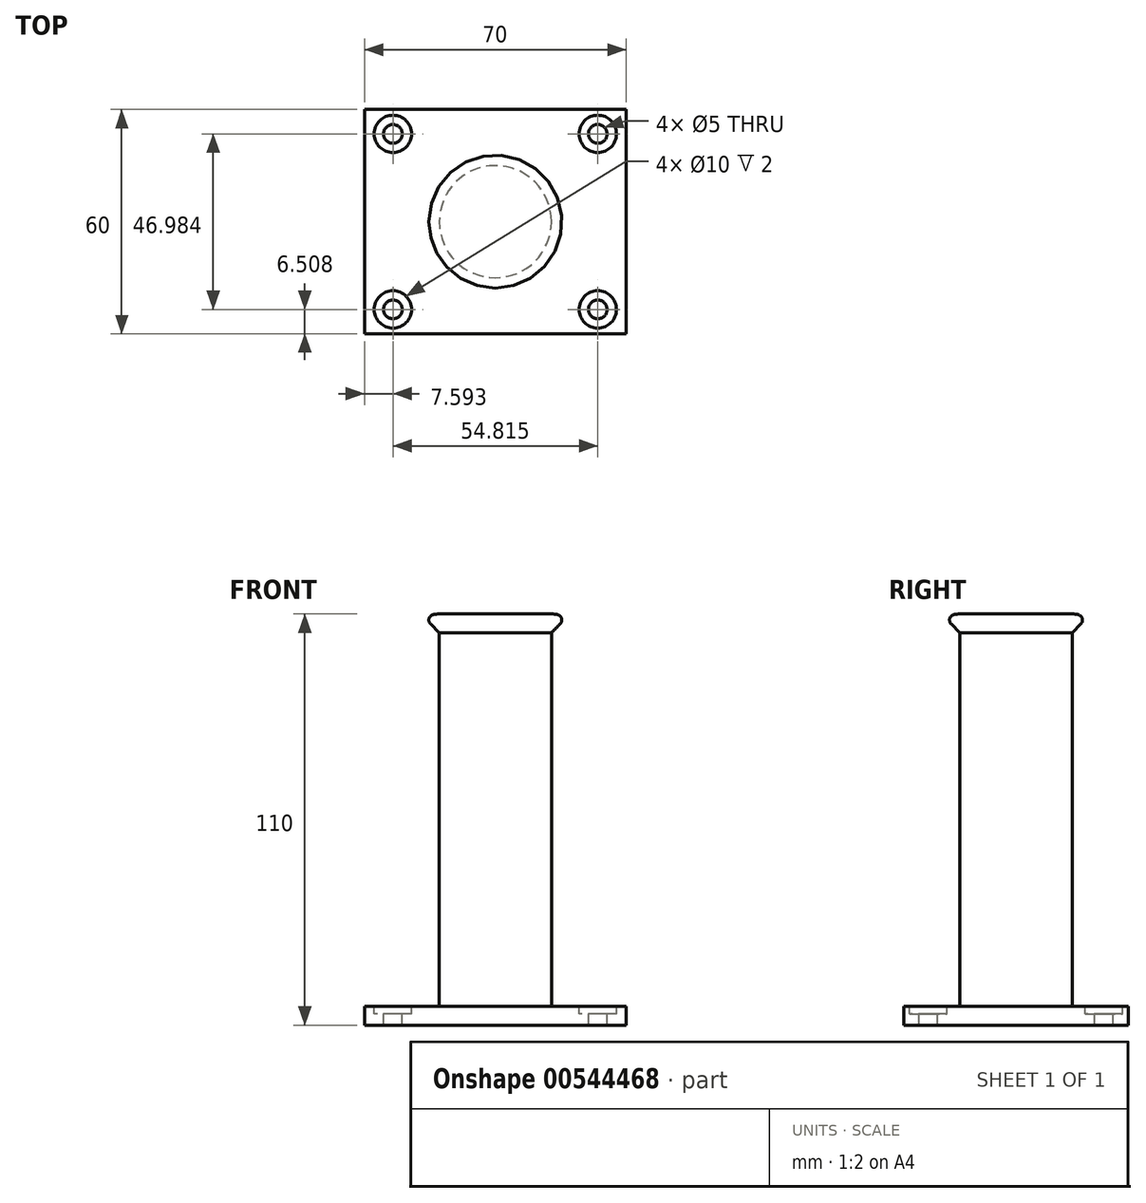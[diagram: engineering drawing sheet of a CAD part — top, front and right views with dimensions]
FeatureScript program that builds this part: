
annotation { "Feature Type Name" : "Feature", "Feature Type Description" : "" }
export const myFeature = defineFeature(function(context is Context, id is Id, definition is map)
    precondition{}
    {
        {
            var Q0;
            Q0=qCreatedBy(makeId("Top.planeOp"),FACE);
            var sketch = newSketch(context, id + "F0", { "sketchPlane" : qUnion([Q0])});
            skLineSegment(sketch, "E0.bottom", {"start": v(35, 30) * mm, "end": v(-35, 30) * mm});
            skLineSegment(sketch, "E0.top", {"start": v(35, -30) * mm, "end": v(-35, -30) * mm});
            skLineSegment(sketch, "E0.left", {"start": v(35, 30) * mm, "end": v(35, -30) * mm});
            skLineSegment(sketch, "E0.right", {"start": v(-35, 30) * mm, "end": v(-35, -30) * mm});
            skPoint(sketch, "E0.middle", {"position": v(0, 0) * mm});
            skCircle(sketch, "E1", {"center": v(0, 0) * mm, "radius": 15 * mm});
            skPoint(sketch, "E2", {"position": v(-27.4, 23.5) * mm});
            skPoint(sketch, "E3", {"position": v(27.4, 23.5) * mm});
            skPoint(sketch, "E4", {"position": v(27.4, -23.5) * mm});
            skPoint(sketch, "E5", {"position": v(-27.4, -23.5) * mm});
            skSolve(sketch);
        }
        {
            var Q0;
            Q0 = qSketchRegion(id + "F0", true);
            extrude(context, id + "F1", {"entities" : qUnion([Q0]), "depth" : 5 * mm, "offsetDistance" : 25 * mm});
        }
        {
            var Q0;
            Q0=makeQuery(id+"F0.imprint","IMPRINT",FACE,{"disambiguationData":[TD([[makeQuery(id+"F0.imprint","IMPRINT",EDGE,{"derivedFrom":sQuery(id+"F0.wireOp",EDGE,"E1")}),1.0]])]});
            extrude(context, id + "F2", {"entities" : qUnion([Q0]), "operationType" : NewBodyOperationType.ADD, "depth" : 105 * mm, "offsetDistance" : 25 * mm});
        }
        {
            var Q0;
            Q0=makeQuery(id+"F2.opExtrude","CAP_FACE",FACE,{"disambiguationData":[OSD([sQuery(id+"F0.wireOp",EDGE,"E1")])],"isStart":false});
            var sketch = newSketch(context, id + "F3", { "sketchPlane" : qUnion([Q0])});
            skCircle(sketch, "E6", {"center": v(0, 0) * mm, "radius": 18.75 * mm});
            skSolve(sketch);
        }
        {
            var Q0;
            Q0=makeQuery(id+"F3.imprint","IMPRINT",FACE,{"disambiguationData":[TD([[makeQuery(id+"F3.imprint","IMPRINT",EDGE,{"derivedFrom":sQuery(id+"F3.wireOp",EDGE,"E6")}),1.0]])]});
            var Q1;
            Q1=makeQuery(id+"F3.imprint","IMPRINT",FACE,{"disambiguationData":[TD([[makeQuery(id+"F3.imprint","IMPRINT",EDGE,{"derivedFrom":makeQuery(id+"F2.opExtrude","CAP_EDGE",EDGE,{"disambiguationData":[OSD([sQuery(id+"F0.wireOp",EDGE,"E1")])],"isStart":false})}),1.0]])]});
            extrude(context, id + "F4", {"entities" : qUnion([Q0, Q1]), "operationType" : NewBodyOperationType.ADD, "depth" : 5 * mm, "offsetDistance" : 25 * mm});
        }
        {
            var Q0;
            Q0=makeQuery(id+"F4.opExtrude","CAP_EDGE",EDGE,{"disambiguationData":[OSD([sQuery(id+"F3.wireOp",EDGE,"E6")])],"isStart":true});
            chamfer(context, id + "F5", {"entities" : qUnion([Q0]), "width" : 3.75 * mm, "tangentPropagation" : true});
        }
        {
            var Q0;
            Q0=makeQuery(id+"F4.opExtrude","CAP_EDGE",EDGE,{"disambiguationData":[OSD([sQuery(id+"F3.wireOp",EDGE,"E6")])],"isStart":false});
            fillet(context, id + "F6", {"entities" : qUnion([Q0]), "radius" : 5 * mm, "allowEdgeOverflow" : false});
        }
        {
            var Q0;
            {var subQ0=sQuery(id+"F3.wireOp",EDGE,"E6");Q0=makeQuery(id+"F6.opFillet","BLEND_EDGE",EDGE,{"blendedFrom":[makeQuery(id+"F4.opExtrude","CAP_EDGE",EDGE,{"disambiguationData":[OSD([subQ0])],"isStart":false}),makeQuery(id+"F5.opChamfer","BLEND_FACE",FACE,{"disambiguationData":[OSD([subQ0])]})],"blendedInto":[makeQuery(id+"F5.opChamfer","BLEND_FACE",FACE,{"disambiguationData":[OSD([subQ0])]})]});}
            fillet(context, id + "F7", {"entities" : qUnion([Q0]), "radius" : 1.5 * mm, "tangentPropagation" : true, "allowEdgeOverflow" : false});
        }
        {
            var Q0;
            Q0=makeQuery(id+"F1.opExtrude","CAP_FACE",FACE,{"disambiguationData":[OSD([sQuery(id+"F0.wireOp",EDGE,"E0.bottom"),sQuery(id+"F0.wireOp",EDGE,"E0.top"),sQuery(id+"F0.wireOp",EDGE,"E0.left"),sQuery(id+"F0.wireOp",EDGE,"E0.right"),sQuery(id+"F0.wireOp",EDGE,"E1")])],"isStart":false});
            var sketch = newSketch(context, id + "F8", { "sketchPlane" : qUnion([Q0])});
            skPoint(sketch, "E7", {"position": v(-27.4, 23.5) * mm});
            skPoint(sketch, "E8", {"position": v(27.4, 23.5) * mm});
            skPoint(sketch, "E9", {"position": v(27.4, -23.5) * mm});
            skPoint(sketch, "E10", {"position": v(-27.4, -23.5) * mm});
            skSolve(sketch);
        }
        {
            var Q0;
            Q0=sQuery(id+"F8.wireOp",VERTEX,"E7");
            var Q1;
            Q1=sQuery(id+"F8.wireOp",VERTEX,"E10");
            var Q2;
            Q2=sQuery(id+"F8.wireOp",VERTEX,"E9");
            var Q3;
            Q3=sQuery(id+"F8.wireOp",VERTEX,"E8");
            var Q4;
            Q4=makeQuery(id+"F1.opExtrude","SWEPT_BODY",BODY,{"disambiguationData":[OSD([sQuery(id+"F0.wireOp",EDGE,"E0.bottom"),sQuery(id+"F0.wireOp",EDGE,"E0.top"),sQuery(id+"F0.wireOp",EDGE,"E0.left"),sQuery(id+"F0.wireOp",EDGE,"E0.right"),sQuery(id+"F0.wireOp",EDGE,"E1")])]});
            hole(context, id + "F9", {"style" : HoleStyle.C_BORE, "endStyle" : HoleEndStyle.BLIND, "holeDiameter" : 5 * mm, "cBoreDiameter" : 10 * mm, "cBoreDepth" : 2 * mm, "holeDepth" : 5 * mm, "isTappedThrough" : true, "tappedDepth" : 12 * mm, "tapClearance" : 3, "startFromSketch" : true, "locations" : qUnion([Q0, Q1, Q2, Q3]), "scope" : qUnion([Q4])});
        }
    });
